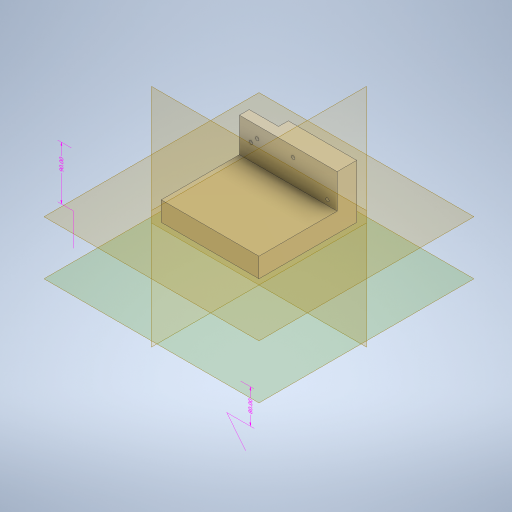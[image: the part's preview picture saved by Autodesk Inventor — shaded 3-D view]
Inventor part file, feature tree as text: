
AUTODESK INVENTOR PART (.ipt)
format: ipt  version: 2023 (Build 270158000, 158)  size: 438,784 bytes
history: native  units: mm
features: sketch x9, extrude x5, other x4, hole x4, plane x4, split x4
ambient origin geometry x8: Origin, YZ Plane, XZ Plane, XY Plane, X Axis, Y Axis, Z Axis, Center Point
bodies: Body1 (feature_tree)
feature tree (30):
  other  "Sólido1"
  other  "Anotaciones"
  extrude  "Extrusión1"  Depth=200.0mm
  hole  "Agujero1"  [1 undecoded]
  extrude  "Extrusión2"  Depth=15.0mm
  extrude  "Extrusión3"  Depth=80.0mm TaperAngle=0.0deg
  extrude  "Extrusión4"  Depth=200.0mm
  extrude  "Extrusión5"  Depth=20.0mm
  hole  "Agujero2"  [1 undecoded]
  plane  "Plano de trabajo1"
  split  "Dividir1"
  plane  "Plano de trabajo2"
  plane  "Plano de trabajo3"
  sketch  "Boceto9"  dims[d37=20.0mm d38=20.0mm]
  plane  "Plano de trabajo4"
  hole  "Agujero3"  [1 undecoded]
  hole  "Agujero4"  [1 undecoded]
  split  "Dividir2"
  split  "Dividir3"
  split  "Dividir4"
  sketch  "Boceto2"  dims[d7=15.0mm d8=200.0mm]
  sketch  "Boceto3"  dims[d9=10.0mm d10=0.0mm]
  sketch  "Boceto4"  dims[d12=1.75mm d13=1.75mm d14=1.75mm d15=1.75mm d16=10.0mm d17=10.0mm d19=30.0mm]
  sketch  "Boceto5"  dims[d20=3.5mm d21=6.0mm d22=4.0mm d23=2.0mm d24=90.0deg d25=8.0mm d26=20.594885mm d27=15.0mm]
  sketch  "Boceto6"  dims[d28=20.0mm d29=80.0mm d30=0.0mm]
  sketch  "Boceto7"  dims[d31=48.0mm d32=200.0mm]
  sketch  "Boceto8"  dims[d33=110.0mm d34=0.0mm d36=20.0mm]
  sketch  "Boceto10"  dims[d39=90.0mm d40=0.0mm d42=10.0mm d43=30.0mm d44=0.0mm d46=1.75mm d47=1.75mm d48=1.75mm d49=1.75mm d50=10.0mm d51=10.0mm d52=15.0mm d56=3.5mm d57=6.0mm d58=4.0mm d59=2.0mm d60=90.0deg d61=8.0mm d62=20.594885mm d63=10.0mm d65=10.0mm d66=10.0mm d67=31.75mm d70=15.0mm d74=200.0mm d78=20.0mm d82=90.0deg d83=10.0mm d84=30.0mm d85=5.0mm d86=5.0mm d87=5.0mm d88=5.0mm d89=20.0mm d91=30.0mm d92=5.0mm d93=5.0mm d94=3.5mm d95=5.0mm d96=5.0mm d97=5.0mm d98=5.0mm d99=5.0mm d100=20.0mm d101=3.5mm d102=6.0mm d103=4.0mm d104=2.0mm d105=90.0deg d106=8.0mm d107=20.594885mm d108=10.0mm d109=30.0mm d110=5.0mm d111=5.0mm d112=5.0mm d113=5.0mm d114=5.0mm d115=5.0mm d116=3.5mm d117=5.0mm d118=5.0mm d119=5.0mm d120=5.0mm d121=5.0mm d122=30.0mm d123=30.0mm d124=3.5mm d125=6.0mm d126=4.0mm d127=2.0mm d128=90.0deg d129=8.0mm d130=20.594885mm d75=1.454734mm d76=6.982969mm d77=80.0mm d79=4.097996mm d80=1.406125mm d81=90.0mm]
  other  "Cota lineal 2"
  other  "Cota lineal 3"
note: 4 required parameter values undecoded (feature->parameter linkage not recoverable at this tier; creation-order binding heuristic only, values carry confidence <= 0.55)
